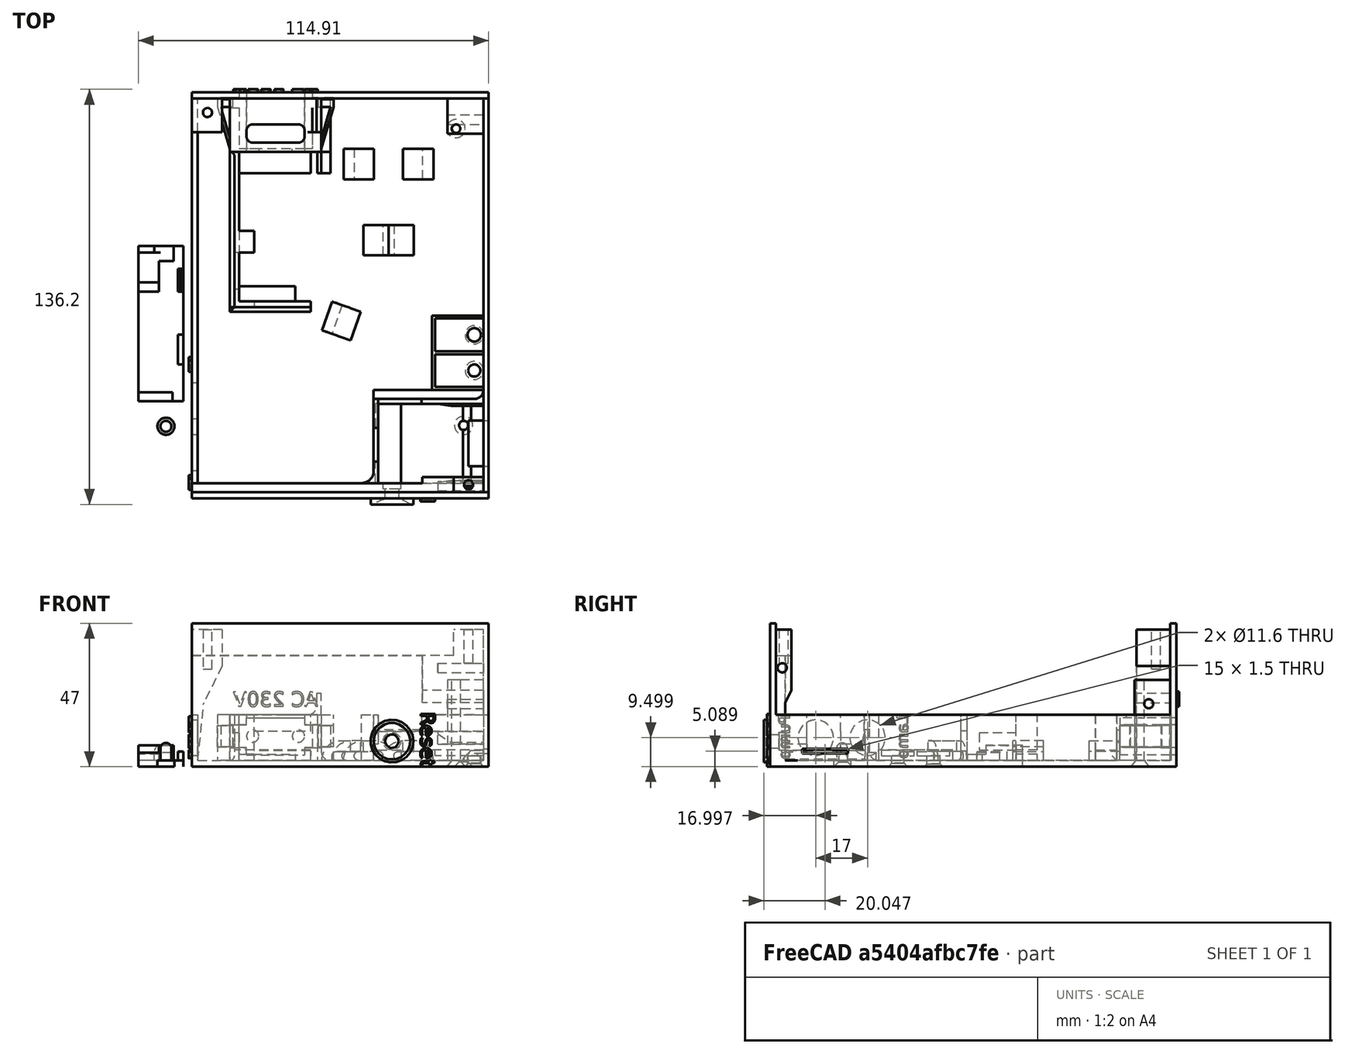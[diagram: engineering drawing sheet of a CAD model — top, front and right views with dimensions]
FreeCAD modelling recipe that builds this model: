
FCSTD DOCUMENT  (FreeCAD 0.18.4R)
Label: tmp2
License: All rights reserved
LicenseURL: http://en.wikipedia.org/wiki/All_rights_reserved
objects: Part::FeaturePython×12, Part::MultiFuse×8, Part::Fuse×4, Part::Feature×3, Part::Part2DObjectPython×2, App::DocumentObjectGroup×2, Part::Cut×1
note: 30 computed .brp shape members not serialized (recipe doc carries the construction recipe); baked Part::Feature solids carry a one-line shape summary decoded from their .brp

FEATURE [Part::MultiFuse] Fusion005002002014004003003002009002010004002003006003008008004007002004008002005011025  label="Pump"
FEATURE [Part::FeaturePython] Slice004_child2001  label="Slice004.008"  # WARN: FeaturePython — macro-defined, semantics opaque (R4)
  FilterType = 1
  Invert = false
  OverrideMaxVal = 0
  WindowFrom = 80
  WindowTo = 100
  items = 2
FEATURE [Part::FeaturePython] Slice004_child3  label="Slice004.3"  # WARN: FeaturePython — macro-defined, semantics opaque (R4)
  FilterType = 1
  Invert = false
  OverrideMaxVal = 0
  WindowFrom = 80
  WindowTo = 100
  items = 3
FEATURE [Part::MultiFuse] Fusion  label="Module"
  Shapes = -> [Slice004_child3,Slice004_child2001]
FEATURE [Part::MultiFuse] Fusion005002002014004003003002009002010004002003006003008008004007002004008002005011023  label="AC230V"
FEATURE [Part::MultiFuse] Fusion005002002014004003003002009002010004002003006003008008004007002004008002005011024  label="Lamp"
FEATURE [Part::Feature] Slice003_child2001001  label="MOSFET001"
  shape: bbox 16.9 x 24.4 x 3.5 mm, 16 faces (baked)
FEATURE [Part::MultiFuse] Fusion005002002014004003003002009002010004002003006003008008004007002004008002005011022  label="Power.Supply"
FEATURE [Part::Cut] Cut001  label="Connector.2"
FEATURE [Part::Feature] Fusion005002002014004003003002009002010004002003006003008008004007002004008002005011019002002002001  label="Frame"
  shape: bbox 97.4 x 131.2 x 45 mm, 79 faces (baked)
FEATURE [Part::Part2DObjectPython] Rectangle  # Draft 2D object (typed FeaturePython)
  ChamferSize = 0
  Columns = 1
  FilletRadius = 0
  Height = 157
  Length = 209
  MakeFace = true
  Placement = pos=(39.7743,-37.3028,-269.94) rot=(1,0,0;1.5708rad)
  Rows = 1
  Support = -> [Fusion005002002014004003003002009002010004002003006003008008004007002004008002005011019002002002001]
FEATURE [Part::FeaturePython] Slice003_child1  label="Slice003.1"  # WARN: FeaturePython — macro-defined, semantics opaque (R4)
  FilterType = 1
  Invert = false
  OverrideMaxVal = 0
  WindowFrom = 80
  WindowTo = 100
  items = 1
FEATURE [Part::Part2DObjectPython] Rectangle001  # Draft 2D object (typed FeaturePython)
  ChamferSize = 0
  Columns = 1
  FilletRadius = 0
  Height = 74.578
  Length = 148.707
  MakeFace = true
  Placement = pos=(30.6227,-163.503,-171.525) rot=(-1,0,0;1.5708rad)
  Rows = 1
FEATURE [Part::FeaturePython] Slice  # WARN: FeaturePython — macro-defined, semantics opaque (R4)
  Base = -> Fusion005002002014004003003002009002010004002003006003008008004007002004008002005011019002002002001
  Mode = 1
  Tolerance = 0
  Tools = -> [Rectangle]
FEATURE [Part::FeaturePython] Slice_child3  label="Slice.3"  # WARN: FeaturePython — macro-defined, semantics opaque (R4)
  Base = -> Slice
  FilterType = 1
  Invert = false
  OverrideMaxVal = 0
  WindowFrom = 80
  WindowTo = 100
  items = 3
FEATURE [Part::FeaturePython] Slice_child1  label="Slice.1"  # WARN: FeaturePython — macro-defined, semantics opaque (R4)
  Base = -> Slice
  FilterType = 1
  Invert = false
  OverrideMaxVal = 0
  WindowFrom = 80
  WindowTo = 100
  items = 1
FEATURE [Part::FeaturePython] Slice_child0  label="Slice.0"  # WARN: FeaturePython — macro-defined, semantics opaque (R4)
  Base = -> Slice
  FilterType = 1
  Invert = false
  OverrideMaxVal = 0
  WindowFrom = 80
  WindowTo = 100
  items = 0
FEATURE [Part::FeaturePython] Slice_child2  label="Slice.2"  # WARN: FeaturePython — macro-defined, semantics opaque (R4)
  Base = -> Slice
  FilterType = 1
  Invert = false
  OverrideMaxVal = 0
  WindowFrom = 80
  WindowTo = 100
  items = 2
FEATURE [App::DocumentObjectGroup] GrExplode_Slice  label="Exploded Slice"
  Group = -> [Slice_child0,Slice_child2,Slice_child3]
FEATURE [Part::FeaturePython] Slice001  # WARN: FeaturePython — macro-defined, semantics opaque (R4)
  Base = -> Slice_child0
  Mode = 1
  Tolerance = 0
  Tools = -> [Rectangle001]
FEATURE [Part::FeaturePython] Slice001_child0  label="Slice001.0"  # WARN: FeaturePython — macro-defined, semantics opaque (R4)
  Base = -> Slice001
  FilterType = 1
  Invert = false
  OverrideMaxVal = 0
  WindowFrom = 80
  WindowTo = 100
  items = 0
FEATURE [Part::FeaturePython] Slice001_child1  label="Slice001.1"  # WARN: FeaturePython — macro-defined, semantics opaque (R4)
  Base = -> Slice001
  FilterType = 1
  Invert = false
  OverrideMaxVal = 0
  WindowFrom = 80
  WindowTo = 100
  items = 1
FEATURE [Part::MultiFuse] Fusion005002002014004003003002009002010004002003006003008008004007002004008002005011019002002002002
  Shapes = -> [Slice001_child1,Slice003_child1]
FEATURE [Part::Fuse] Fusion005002002014004003003002009002010004002003006003008008004007002004008002005011019002002002004
  Base = -> Slice_child1
  Tool = -> Fusion005002002014004003003002009002010004002003006003008008004007002004008002005011019002002002002
FEATURE [Part::FeaturePython] Slice001_child2  label="Slice001.2"  # WARN: FeaturePython — macro-defined, semantics opaque (R4)
  Base = -> Slice001
  FilterType = 1
  Invert = false
  OverrideMaxVal = 0
  WindowFrom = 80
  WindowTo = 100
  items = 2
FEATURE [Part::Fuse] Fusion005002002014004003003002009002010004002003006003008008004007002004008002005011019002002002003
  Base = -> Slice001_child0
  Tool = -> Slice001_child2
FEATURE [Part::Fuse] Fusion005002002014004003003002009002010004002003006003008008004007002004008002005011019002002002005
  Base = -> Fusion005002002014004003003002009002010004002003006003008008004007002004008002005011019002002002003
  Tool = -> Fusion005002002014004003003002009002010004002003006003008008004007002004008002005011019002002002004
FEATURE [Part::MultiFuse] Fusion005002002014004003003002009002010004002003006003008008004007002004008002005011020  label="Bottot.2"
FEATURE [Part::Fuse] Fusion005002002014004003003002009002010004002003006003008008004007002004008002005011019002002002006
  Base = -> Fusion005002002014004003003002009002010004002003006003008008004007002004008002005011020
  Tool = -> Fusion005002002014004003003002009002010004002003006003008008004007002004008002005011019002002002005
FEATURE [App::DocumentObjectGroup] GrExplode_Slice001  label="Exploded Slice001"
  Group = -> [Fusion005002002014004003003002009002010004002003006003008008004007002004008002005011019002002002006]
FEATURE [Part::MultiFuse] Fusion005002002014004003003002009002010004002003006003008008004007002004008002003
  Placement = pos=(371.865,-232.312,-185.367) rot=(0,0,1;0rad)
FEATURE [Part::Feature] Fusion005002002014004003003002009002010004002003006003008008004007002004008002005001  label="Fusion005002002014004003003002009002010004002003006003008008004007002004008002006"
  shape: bbox 14.8 x 50.9 x 7 mm, 30 faces (baked)
